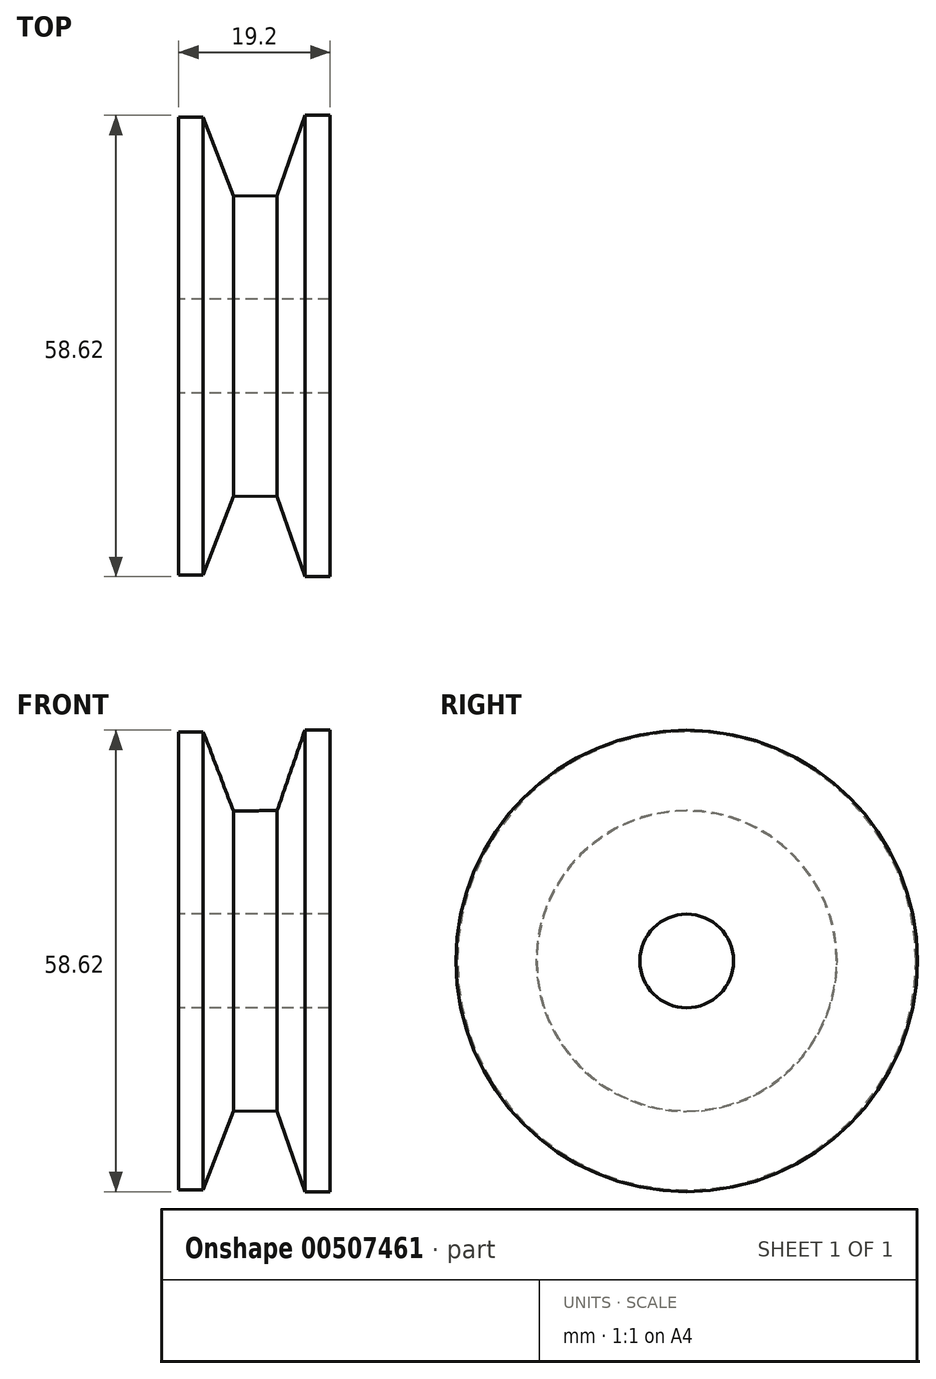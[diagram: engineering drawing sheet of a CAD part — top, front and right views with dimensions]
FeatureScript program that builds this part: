
annotation { "Feature Type Name" : "Feature", "Feature Type Description" : "" }
export const myFeature = defineFeature(function(context is Context, id is Id, definition is map)
    precondition{}
    {
        {
            var Q0;
            Q0=qCreatedBy(makeId("Front.planeOp"),FACE);
            var sketch = newSketch(context, id + "F0", { "sketchPlane" : qUnion([Q0])});
            skLineSegment(sketch, "E0", {"start": v(0, 0) * mm, "end": v(19.2, 0) * mm});
            skLineSegment(sketch, "E1", {"start": v(0, 0) * mm, "end": v(0, 29.1) * mm});
            skLineSegment(sketch, "E2", {"start": v(19.2, 0) * mm, "end": v(19.2, 29.3) * mm});
            skLineSegment(sketch, "E3", {"start": v(0, 29.1) * mm, "end": v(3.1, 29.1) * mm});
            skLineSegment(sketch, "E4", {"start": v(19.2, 29.3) * mm, "end": v(16.02, 29.3) * mm});
            skLineSegment(sketch, "E5", {"start": v(16.02, 29.3) * mm, "end": v(12.5, 19.12) * mm});
            skLineSegment(sketch, "E6", {"start": v(12.5, 19.12) * mm, "end": v(12.5, 0) * mm});
            skLineSegment(sketch, "E7", {"start": v(3.1, 29.1) * mm, "end": v(6.95, 19.03) * mm});
            skLineSegment(sketch, "E8", {"start": v(6.95, 19.03) * mm, "end": v(6.95, 0) * mm});
            skLineSegment(sketch, "E9", {"start": v(16.02, 29.3) * mm, "end": v(16.02, 0) * mm});
            skLineSegment(sketch, "E10", {"start": v(3.1, 29.1) * mm, "end": v(3.1, 0) * mm});
            skPoint(sketch, "E11.end.orphan", {"position": v(3.1, 19.03) * mm});
            skLineSegment(sketch, "E12", {"start": v(6.95, 19.03) * mm, "end": v(12.5, 19.12) * mm});
            skSolve(sketch);
        }
        {
            var Q0;
            {var subQ0=sQuery(id+"F0.wireOp",EDGE,"E1");Q0=makeQuery(id+"F0.imprint","IMPRINT",FACE,{"disambiguationData":[TD([[makeQuery(id+"F0.imprint","IMPRINT",EDGE,{"derivedFrom":subQ0}),-1.0]])]});}
            var Q1;
            Q1=makeQuery(id+"F0.imprint","IMPRINT",FACE,{"disambiguationData":[TD([[makeQuery(id+"F0.imprint","IMPRINT",EDGE,{"derivedFrom":sQuery(id+"F0.wireOp",EDGE,"E7")}),-1.0]])]});
            var Q2;
            {var subQ0=sQuery(id+"F0.wireOp",EDGE,"E6");Q2=makeQuery(id+"F0.imprint","IMPRINT",FACE,{"disambiguationData":[TD([[makeQuery(id+"F0.imprint","IMPRINT",EDGE,{"derivedFrom":subQ0}),-1.0]])]});}
            var Q3;
            Q3=makeQuery(id+"F0.imprint","IMPRINT",FACE,{"disambiguationData":[TD([[makeQuery(id+"F0.imprint","IMPRINT",EDGE,{"derivedFrom":sQuery(id+"F0.wireOp",EDGE,"E5")}),1.0]])]});
            var Q4;
            {var subQ0=sQuery(id+"F0.wireOp",EDGE,"E2");Q4=makeQuery(id+"F0.imprint","IMPRINT",FACE,{"disambiguationData":[TD([[makeQuery(id+"F0.imprint","IMPRINT",EDGE,{"derivedFrom":subQ0}),1.0]])]});}
            var Q5;
            Q5=sQuery(id+"F0.wireOp",EDGE,"E0");
            revolve(context, id + "F1", {"entities" : qUnion([Q0, Q1, Q2, Q3, Q4]), "axis" : qUnion([Q5]), "revolveType" : RevolveType.FULL});
        }
        {
            var Q0;
            Q0=qCreatedBy(makeId("Right.planeOp"),FACE);
            var sketch = newSketch(context, id + "F2", { "sketchPlane" : qUnion([Q0])});
            skCircle(sketch, "E13", {"center": v(0, 0) * mm, "radius": 5.95 * mm});
            skSolve(sketch);
        }
        {
            var Q0;
            Q0 = qSketchRegion(id + "F2", true);
            extrude(context, id + "F3", {"entities" : qUnion([Q0]), "operationType" : NewBodyOperationType.REMOVE, "depth" : 25 * mm});
        }
    });
